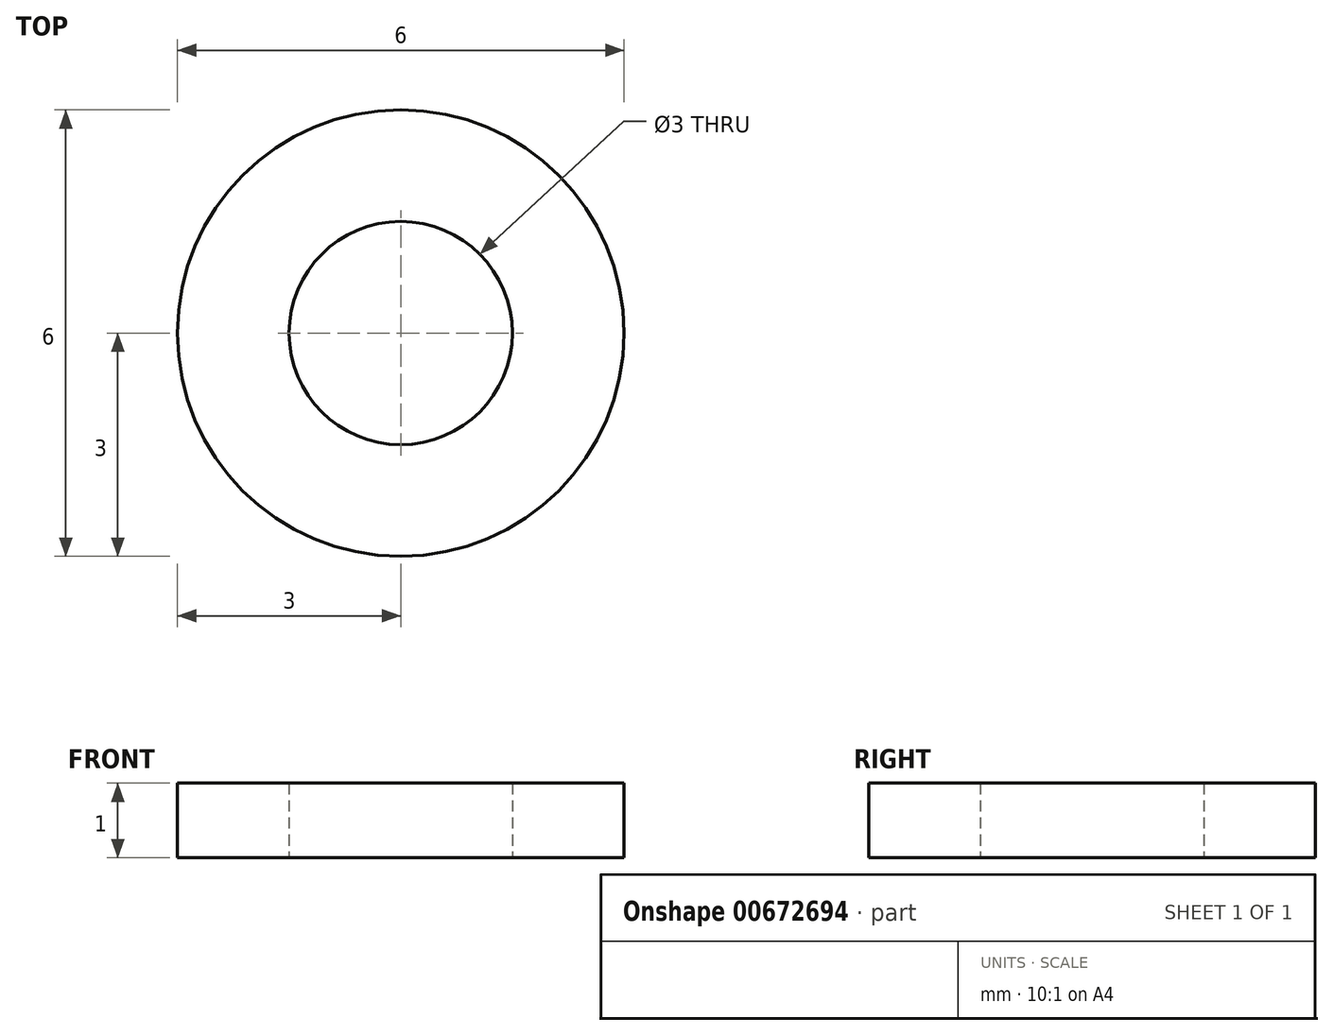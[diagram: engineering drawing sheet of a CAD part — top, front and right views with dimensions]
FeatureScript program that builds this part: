
annotation { "Feature Type Name" : "Feature", "Feature Type Description" : "" }
export const myFeature = defineFeature(function(context is Context, id is Id, definition is map)
    precondition{}
    {
        {
            var Q0;
            Q0=qCreatedBy(makeId("Top.planeOp"),FACE);
            var sketch = newSketch(context, id + "F0", { "sketchPlane" : qUnion([Q0])});
            skCircle(sketch, "E0", {"center": v(0, 0) * mm, "radius": 3 * mm});
            skCircle(sketch, "E1", {"center": v(0, 0) * mm, "radius": 1.5 * mm});
            skSolve(sketch);
        }
        {
            var Q0;
            Q0=makeQuery(id+"F0.imprint","IMPRINT",FACE,{"disambiguationData":[TD([[makeQuery(id+"F0.imprint","IMPRINT",EDGE,{"derivedFrom":sQuery(id+"F0.wireOp",EDGE,"E0")}),1.0]])]});
            extrude(context, id + "F1", {"entities" : qUnion([Q0]), "depth" : 1 * mm, "offsetDistance" : 25 * mm});
        }
    });
